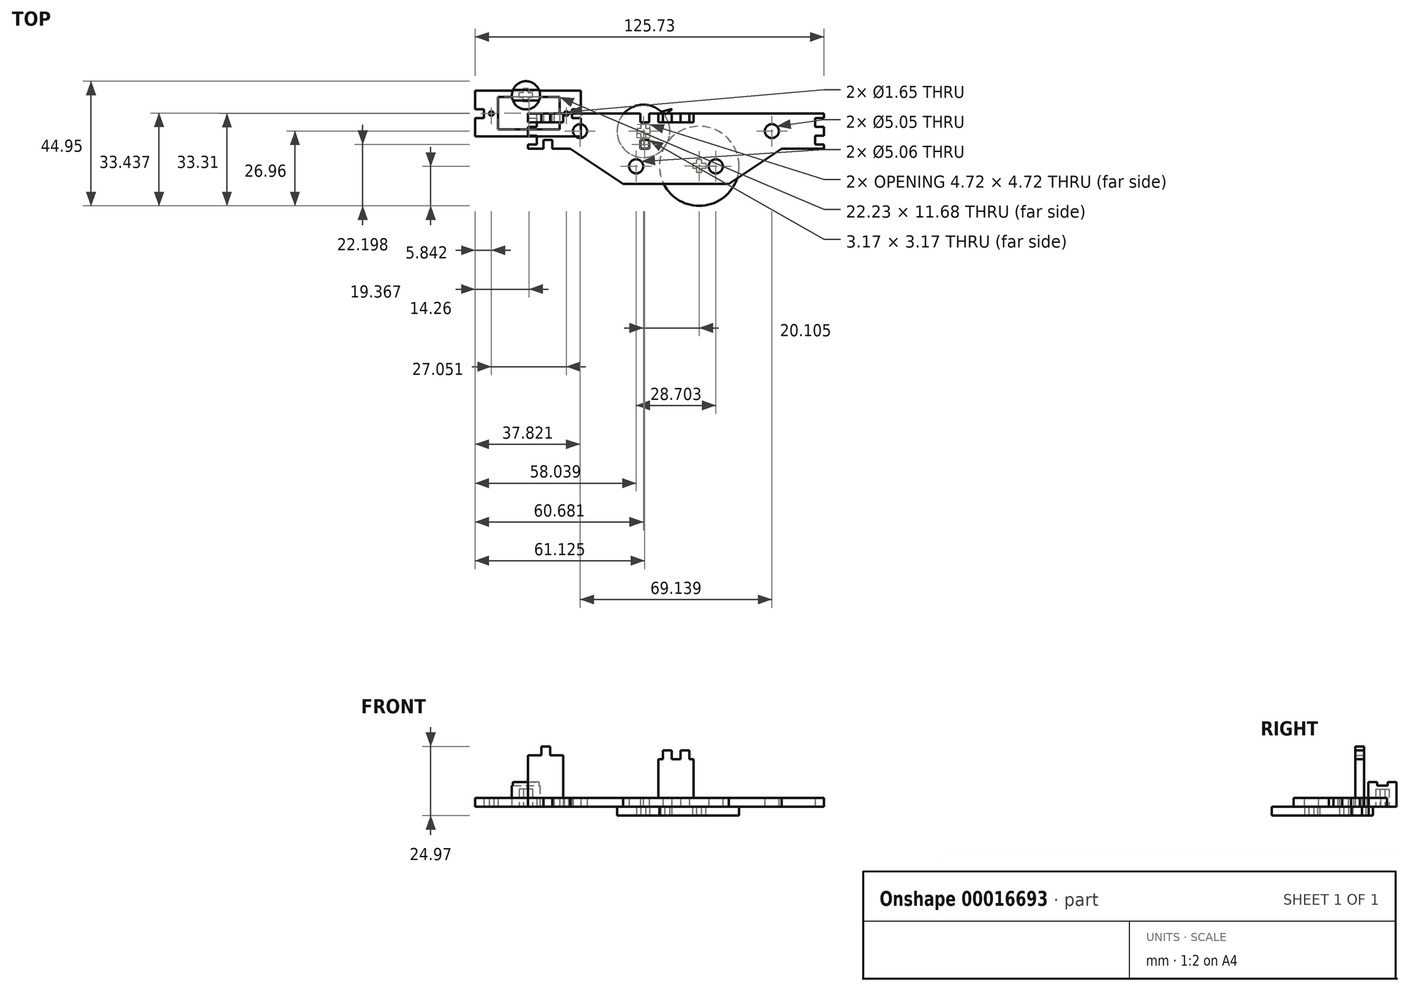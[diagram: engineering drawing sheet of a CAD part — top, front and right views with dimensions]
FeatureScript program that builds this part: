
annotation { "Feature Type Name" : "Feature", "Feature Type Description" : "" }
export const myFeature = defineFeature(function(context is Context, id is Id, definition is map)
    precondition{}
    {
        {
            var Q0;
            Q0=qCreatedBy(makeId("Top.planeOp"),FACE);
            var sketch = newSketch(context, id + "F0", { "sketchPlane" : qUnion([Q0])});
            skLineSegment(sketch, "E0.bottom", {"start": v(0, 0) * mm, "end": v(5.56, 0) * mm});
            skLineSegment(sketch, "E0.top", {"start": v(0, -12.7) * mm, "end": v(5.56, -12.7) * mm});
            skLineSegment(sketch, "E0.left", {"start": v(0, 0) * mm, "end": v(0, -12.7) * mm});
            skLineSegment(sketch, "E0.right", {"start": v(106.68, 0) * mm, "end": v(106.68, -12.7) * mm});
            skPoint(sketch, "E1", {"position": v(18.77, -6.35) * mm});
            skPoint(sketch, "E2", {"position": v(87.9, -6.35) * mm});
            skLineSegment(sketch, "E3", {"start": v(0, -6.35) * mm, "end": v(106.68, -6.35) * mm, "construction": true});
            skLineSegment(sketch, "E4.rect.bottom", {"start": v(19.66, -8.71) * mm, "end": v(17.88, -8.71) * mm});
            skLineSegment(sketch, "E4.rect.top", {"start": v(19.66, -3.99) * mm, "end": v(17.88, -3.99) * mm});
            skLineSegment(sketch, "E4.rect.left", {"start": v(19.66, -8.71) * mm, "end": v(19.66, -3.99) * mm});
            skLineSegment(sketch, "E4.rect.right", {"start": v(17.88, -8.71) * mm, "end": v(17.88, -3.99) * mm});
            skPoint(sketch, "E5.rect.middle", {"position": v(110.77, -6.35) * mm});
            skCircle(sketch, "E6", {"center": v(18.77, -6.35) * mm, "radius": 2.52 * mm});
            skPoint(sketch, "E7", {"position": v(53.34, -6.35) * mm});
            skLineSegment(sketch, "E8", {"start": v(15.24, -12.7) * mm, "end": v(34.3, -25.4) * mm});
            skLineSegment(sketch, "E9", {"start": v(34.3, -25.4) * mm, "end": v(72.4, -25.4) * mm});
            skLineSegment(sketch, "E10", {"start": v(72.4, -25.4) * mm, "end": v(91.44, -12.7) * mm});
            skLineSegment(sketch, "E11", {"start": v(18.77, -6.35) * mm, "end": v(87.9, -6.35) * mm});
            skCircle(sketch, "E12", {"center": v(38.99, -19.05) * mm, "radius": 2.53 * mm});
            skLineSegment(sketch, "E13", {"start": v(53.34, 9.16) * mm, "end": v(53.34, -37.34) * mm, "construction": true});
            skCircle(sketch, "E14.0.MirrorC", {"center": v(67.7, -19.05) * mm, "radius": 2.53 * mm});
            skCircle(sketch, "E15.0.MirrorC", {"center": v(87.9, -6.35) * mm, "radius": 2.52 * mm});
            skLineSegment(sketch, "E16.bottom", {"start": v(0, -1.59) * mm, "end": v(3.18, -1.59) * mm});
            skLineSegment(sketch, "E16.top", {"start": v(0, -4.76) * mm, "end": v(3.17, -4.76) * mm});
            skLineSegment(sketch, "E16.left", {"start": v(0, -1.59) * mm, "end": v(0, -4.76) * mm});
            skLineSegment(sketch, "E16.right", {"start": v(3.18, -1.59) * mm, "end": v(3.18, -4.76) * mm});
            skLineSegment(sketch, "E17.0.MirrorCS", {"start": v(0, -7.94) * mm, "end": v(3.17, -7.94) * mm});
            skLineSegment(sketch, "E18.0.MirrorCS", {"start": v(3.17, -11.11) * mm, "end": v(3.17, -7.94) * mm});
            skLineSegment(sketch, "E19.0.MirrorCS", {"start": v(0, -11.11) * mm, "end": v(3.18, -11.11) * mm});
            skLineSegment(sketch, "E20.0.MirrorCS", {"start": v(0, -11.11) * mm, "end": v(0, -7.94) * mm});
            skLineSegment(sketch, "E21.0.MirrorCS", {"start": v(103.5, -1.59) * mm, "end": v(103.5, -4.76) * mm});
            skLineSegment(sketch, "E22.0.MirrorCS", {"start": v(106.68, -1.59) * mm, "end": v(103.5, -1.59) * mm});
            skLineSegment(sketch, "E23.0.MirrorCS", {"start": v(106.68, -4.76) * mm, "end": v(103.5, -4.76) * mm});
            skLineSegment(sketch, "E24.0.MirrorCS", {"start": v(106.68, -1.59) * mm, "end": v(106.68, -4.76) * mm});
            skLineSegment(sketch, "E25.0.MirrorCS", {"start": v(106.68, -7.94) * mm, "end": v(103.5, -7.94) * mm});
            skLineSegment(sketch, "E26.0.MirrorCS", {"start": v(103.5, -11.11) * mm, "end": v(103.5, -7.94) * mm});
            skLineSegment(sketch, "E27.0.MirrorCS", {"start": v(106.68, -11.11) * mm, "end": v(103.5, -11.11) * mm});
            skLineSegment(sketch, "E28.0.MirrorCS", {"start": v(106.68, -11.11) * mm, "end": v(106.68, -7.94) * mm});
            skLineSegment(sketch, "E29", {"start": v(5.56, 0) * mm, "end": v(5.56, -3.18) * mm});
            skLineSegment(sketch, "E30", {"start": v(5.56, -3.18) * mm, "end": v(8.74, -3.18) * mm});
            skLineSegment(sketch, "E31", {"start": v(8.74, -3.18) * mm, "end": v(8.74, 0) * mm});
            skLineSegment(sketch, "E32", {"start": v(8.74, -12.7) * mm, "end": v(8.74, -9.52) * mm});
            skLineSegment(sketch, "E33", {"start": v(8.74, -9.52) * mm, "end": v(5.56, -9.52) * mm});
            skLineSegment(sketch, "E34", {"start": v(5.56, -9.52) * mm, "end": v(5.56, -12.7) * mm});
            skLineSegment(sketch, "E35.trimOffspring", {"start": v(8.74, 0) * mm, "end": v(40.49, 0) * mm});
            skLineSegment(sketch, "E36.trimOffspring", {"start": v(8.74, -12.7) * mm, "end": v(106.68, -12.7) * mm});
            skLineSegment(sketch, "E37", {"start": v(40.49, 0) * mm, "end": v(40.49, -3.18) * mm});
            skLineSegment(sketch, "E38", {"start": v(40.49, -3.18) * mm, "end": v(43.66, -3.18) * mm});
            skLineSegment(sketch, "E39", {"start": v(43.66, -3.18) * mm, "end": v(43.66, 0) * mm});
            skLineSegment(sketch, "E40", {"start": v(40.49, -12.7) * mm, "end": v(40.49, -9.52) * mm});
            skLineSegment(sketch, "E41", {"start": v(40.49, -9.52) * mm, "end": v(43.66, -9.52) * mm});
            skLineSegment(sketch, "E42", {"start": v(43.66, -9.52) * mm, "end": v(43.66, -12.7) * mm});
            skLineSegment(sketch, "E43.trimOffspring", {"start": v(43.66, 0) * mm, "end": v(106.68, 0) * mm});
            skLineSegment(sketch, "E44.top", {"start": v(51.75, -3.17) * mm, "end": v(48.58, -3.17) * mm});
            skLineSegment(sketch, "E44.left", {"start": v(51.75, 0) * mm, "end": v(51.75, -3.17) * mm});
            skLineSegment(sketch, "E44.right", {"start": v(48.58, 0) * mm, "end": v(48.58, -3.17) * mm});
            skLineSegment(sketch, "E45.top", {"start": v(54.93, -3.17) * mm, "end": v(58.1, -3.17) * mm});
            skLineSegment(sketch, "E45.left", {"start": v(54.93, 0) * mm, "end": v(54.93, -3.17) * mm});
            skLineSegment(sketch, "E45.right", {"start": v(58.1, 0) * mm, "end": v(58.1, -3.17) * mm});
            skPoint(sketch, "E46", {"position": v(53.34, 0) * mm});
            skSolve(sketch);
        }
        {
            var Q0;
            {var subQ3=sQuery(id+"F0.wireOp",EDGE,"E8");var subQ35=sQuery(id+"F0.wireOp",EDGE,"E0.bottom");Q0=qUnion([makeQuery(id+"F0.imprint","IMPRINT",FACE,{"disambiguationData":[TD([[makeQuery(id+"F0.imprint","IMPRINT",EDGE,{"derivedFrom":subQ3}),1.0]])]}),makeQuery(id+"F0.imprint","IMPRINT",FACE,{"disambiguationData":[TD([[makeQuery(id+"F0.imprint","IMPRINT",EDGE,{"derivedFrom":subQ35}),-1.0]])]})]);}
            extrude(context, id + "F1", {"entities" : qUnion([Q0]), "depth" : 3.17 * mm});
        }
        {
            var Q0;
            Q0=qCreatedBy(makeId("Top.planeOp"),FACE);
            var sketch = newSketch(context, id + "F2", { "sketchPlane" : qUnion([Q0])});
            skCircle(sketch, "E47", {"center": v(41.63, -6.35) * mm, "radius": 9.53 * mm});
            skLineSegment(sketch, "E48", {"start": v(49.38, -0.81) * mm, "end": v(51.92, 1.7) * mm});
            skLineSegment(sketch, "E49", {"start": v(51.92, 1.7) * mm, "end": v(48.03, 0.7) * mm});
            skLineSegment(sketch, "E50.rect.bottom", {"start": v(42.52, -8.71) * mm, "end": v(40.74, -8.71) * mm});
            skLineSegment(sketch, "E50.rect.top", {"start": v(42.52, -3.99) * mm, "end": v(40.74, -3.99) * mm});
            skLineSegment(sketch, "E50.rect.left", {"start": v(42.52, -8.71) * mm, "end": v(42.52, -3.99) * mm});
            skLineSegment(sketch, "E50.rect.right", {"start": v(40.74, -8.71) * mm, "end": v(40.74, -3.99) * mm});
            skLineSegment(sketch, "E51.rect.bottom", {"start": v(44, -5.46) * mm, "end": v(39.27, -5.46) * mm});
            skLineSegment(sketch, "E51.rect.top", {"start": v(44, -7.24) * mm, "end": v(39.27, -7.24) * mm});
            skLineSegment(sketch, "E51.rect.left", {"start": v(44, -5.46) * mm, "end": v(44, -7.24) * mm});
            skLineSegment(sketch, "E51.rect.right", {"start": v(39.27, -5.46) * mm, "end": v(39.27, -7.24) * mm});
            skSolve(sketch);
        }
        {
            var Q0;
            Q0=makeQuery(id+"F2.imprint","IMPRINT",FACE,{"disambiguationData":[TD([[makeQuery(id+"F2.imprint","IMPRINT",EDGE,{"derivedFrom":sQuery(id+"F2.wireOp",EDGE,"56dfebe2-708b-410e-807d-a486b5c591f2.0")}),-1.0]])]});
            var Q1;
            {var subQ11=sQuery(id+"F2.wireOp",EDGE,"E50.rect.bottom");Q1=makeQuery(id+"F2.imprint","IMPRINT",FACE,{"disambiguationData":[TD([[makeQuery(id+"F2.imprint","IMPRINT",EDGE,{"derivedFrom":subQ11}),1.0]])]});}
            var Q2;
            {var subQ1=sQuery(id+"F2.wireOp",EDGE,"E48");Q2=makeQuery(id+"F2.imprint","IMPRINT",FACE,{"disambiguationData":[TD([[makeQuery(id+"F2.imprint","IMPRINT",EDGE,{"derivedFrom":subQ1}),1.0]])]});}
            extrude(context, id + "F3", {"entities" : qUnion([Q0, Q1, Q2]), "oppositeDirection" : true, "depth" : 3.17 * mm});
        }
        {
            var Q0;
            Q0=qCreatedBy(makeId("Top.planeOp"),FACE);
            var sketch = newSketch(context, id + "F4", { "sketchPlane" : qUnion([Q0])});
            skLineSegment(sketch, "E52.rect.bottom", {"start": v(62.62, -21.32) * mm, "end": v(60.85, -21.32) * mm});
            skLineSegment(sketch, "E52.rect.top", {"start": v(62.62, -16.6) * mm, "end": v(60.85, -16.6) * mm});
            skLineSegment(sketch, "E52.rect.left", {"start": v(62.62, -21.32) * mm, "end": v(62.62, -16.6) * mm});
            skLineSegment(sketch, "E52.rect.right", {"start": v(60.85, -21.32) * mm, "end": v(60.85, -16.6) * mm});
            skPoint(sketch, "E52.rect.middle", {"position": v(61.74, -18.96) * mm});
            skLineSegment(sketch, "E53.rect.bottom", {"start": v(64.1, -18.07) * mm, "end": v(59.37, -18.07) * mm});
            skLineSegment(sketch, "E53.rect.top", {"start": v(64.1, -19.85) * mm, "end": v(59.37, -19.85) * mm});
            skLineSegment(sketch, "E53.rect.left", {"start": v(64.1, -18.07) * mm, "end": v(64.1, -19.85) * mm});
            skLineSegment(sketch, "E53.rect.right", {"start": v(59.37, -18.07) * mm, "end": v(59.37, -19.85) * mm});
            skCircle(sketch, "E54", {"center": v(61.74, -18.96) * mm, "radius": 14.35 * mm});
            skSolve(sketch);
        }
        {
            var Q0;
            {var subQ11=sQuery(id+"F4.wireOp",EDGE,"E52.rect.bottom");Q0=makeQuery(id+"F4.imprint","IMPRINT",FACE,{"disambiguationData":[TD([[makeQuery(id+"F4.imprint","IMPRINT",EDGE,{"derivedFrom":subQ11}),1.0]])]});}
            extrude(context, id + "F5", {"entities" : qUnion([Q0]), "oppositeDirection" : true, "depth" : 3.17 * mm});
        }
        {
            var Q0;
            Q0=qCreatedBy(makeId("Top.planeOp"),FACE);
            var sketch = newSketch(context, id + "F6", { "sketchPlane" : qUnion([Q0])});
            skCircle(sketch, "E55", {"center": v(-0.7, 6.56) * mm, "radius": 5.08 * mm});
            skLineSegment(sketch, "E56.rect.bottom", {"start": v(1.7, 5.67) * mm, "end": v(-3.12, 5.67) * mm});
            skLineSegment(sketch, "E56.rect.top", {"start": v(1.7, 7.45) * mm, "end": v(-3.12, 7.45) * mm});
            skLineSegment(sketch, "E56.rect.left", {"start": v(1.7, 5.67) * mm, "end": v(1.7, 7.45) * mm});
            skLineSegment(sketch, "E56.rect.right", {"start": v(-3.12, 5.67) * mm, "end": v(-3.12, 7.45) * mm});
            skLineSegment(sketch, "E57.rect.bottom", {"start": v(0.18, 4.15) * mm, "end": v(-1.6, 4.15) * mm});
            skLineSegment(sketch, "E57.rect.top", {"start": v(0.18, 8.97) * mm, "end": v(-1.6, 8.97) * mm});
            skLineSegment(sketch, "E57.rect.left", {"start": v(0.18, 4.15) * mm, "end": v(0.18, 8.97) * mm});
            skLineSegment(sketch, "E57.rect.right", {"start": v(-1.6, 4.15) * mm, "end": v(-1.6, 8.97) * mm});
            skSolve(sketch);
        }
        {
            var Q0;
            Q0=makeQuery(id+"F6.imprint","IMPRINT",FACE,{"disambiguationData":[TD([[makeQuery(id+"F6.imprint","IMPRINT",EDGE,{"derivedFrom":sQuery(id+"F6.wireOp",EDGE,"E55")}),1.0]])]});
            var Q1;
            {var subQ5=sQuery(id+"F6.wireOp",EDGE,"E56.rect.right");Q1=makeQuery(id+"F6.imprint","IMPRINT",FACE,{"disambiguationData":[TD([[makeQuery(id+"F6.imprint","IMPRINT",EDGE,{"derivedFrom":subQ5}),-1.0]])]});}
            var Q2;
            {var subQ3=sQuery(id+"F6.wireOp",EDGE,"E57.rect.top");Q2=makeQuery(id+"F6.imprint","IMPRINT",FACE,{"disambiguationData":[TD([[makeQuery(id+"F6.imprint","IMPRINT",EDGE,{"derivedFrom":subQ3}),1.0]])]});}
            var Q3;
            {var subQ3=sQuery(id+"F6.wireOp",EDGE,"E56.rect.bottom");var subQ5=sQuery(id+"F6.wireOp",EDGE,"E57.rect.left");var subQ7=makeQuery(id+"F6.imprint","INTERSECT",VERTEX,{"derivedFrom":[subQ3,subQ5]});Q3=makeQuery(id+"F6.imprint","IMPRINT",FACE,{"disambiguationData":[TD([[makeQuery(id+"F6.imprint","IMPRINT",EDGE,{"disambiguationData":[TD([[subQ7,-1.0]])],"derivedFrom":subQ3}),-1.0]])]});}
            var Q4;
            {var subQ3=sQuery(id+"F6.wireOp",EDGE,"E57.rect.bottom");Q4=makeQuery(id+"F6.imprint","IMPRINT",FACE,{"disambiguationData":[TD([[makeQuery(id+"F6.imprint","IMPRINT",EDGE,{"derivedFrom":subQ3}),-1.0]])]});}
            var Q5;
            {var subQ5=sQuery(id+"F6.wireOp",EDGE,"E56.rect.left");Q5=makeQuery(id+"F6.imprint","IMPRINT",FACE,{"disambiguationData":[TD([[makeQuery(id+"F6.imprint","IMPRINT",EDGE,{"derivedFrom":subQ5}),1.0]])]});}
            extrude(context, id + "F7", {"entities" : qUnion([Q0, Q1, Q2, Q3, Q4, Q5]), "depth" : 8.9 * mm});
        }
        {
            var Q0;
            {var subQ5=sQuery(id+"F6.wireOp",EDGE,"E56.rect.right");Q0=makeQuery(id+"F6.imprint","IMPRINT",FACE,{"disambiguationData":[TD([[makeQuery(id+"F6.imprint","IMPRINT",EDGE,{"derivedFrom":subQ5}),-1.0]])]});}
            var Q1;
            {var subQ3=sQuery(id+"F6.wireOp",EDGE,"E57.rect.top");Q1=makeQuery(id+"F6.imprint","IMPRINT",FACE,{"disambiguationData":[TD([[makeQuery(id+"F6.imprint","IMPRINT",EDGE,{"derivedFrom":subQ3}),1.0]])]});}
            var Q2;
            {var subQ3=sQuery(id+"F6.wireOp",EDGE,"E56.rect.bottom");var subQ5=sQuery(id+"F6.wireOp",EDGE,"E57.rect.left");var subQ7=makeQuery(id+"F6.imprint","INTERSECT",VERTEX,{"derivedFrom":[subQ3,subQ5]});Q2=makeQuery(id+"F6.imprint","IMPRINT",FACE,{"disambiguationData":[TD([[makeQuery(id+"F6.imprint","IMPRINT",EDGE,{"disambiguationData":[TD([[subQ7,-1.0]])],"derivedFrom":subQ3}),-1.0]])]});}
            var Q3;
            {var subQ3=sQuery(id+"F6.wireOp",EDGE,"E57.rect.bottom");Q3=makeQuery(id+"F6.imprint","IMPRINT",FACE,{"disambiguationData":[TD([[makeQuery(id+"F6.imprint","IMPRINT",EDGE,{"derivedFrom":subQ3}),-1.0]])]});}
            var Q4;
            {var subQ5=sQuery(id+"F6.wireOp",EDGE,"E56.rect.left");Q4=makeQuery(id+"F6.imprint","IMPRINT",FACE,{"disambiguationData":[TD([[makeQuery(id+"F6.imprint","IMPRINT",EDGE,{"derivedFrom":subQ5}),1.0]])]});}
            extrude(context, id + "F8", {"entities" : qUnion([Q0, Q1, Q2, Q3, Q4]), "operationType" : NewBodyOperationType.REMOVE, "depth" : 6.35 * mm});
        }
        {
            var Q0;
            Q0=makeQuery(id+"F7.opExtrude","CAP_FACE",FACE,{"disambiguationData":[OSD([sQuery(id+"F6.wireOp",EDGE,"E55")])],"isStart":false});
            var sketch = newSketch(context, id + "F9", { "sketchPlane" : qUnion([Q0])});
            skPoint(sketch, "E58.0", {"position": v(0, 0) * mm});
            skLineSegment(sketch, "E59.rect.bottom", {"start": v(-5.42, 8.47) * mm, "end": v(4, 8.47) * mm});
            skLineSegment(sketch, "E59.rect.top", {"start": v(-5.42, 4.66) * mm, "end": v(4, 4.66) * mm});
            skPoint(sketch, "E59.rect.middle", {"position": v(-0.7, 6.56) * mm});
            skArc(sketch, "E60.0", {"start": v(4, 4.66) * mm, "mid": v(4.37, 6.56) * mm, "end": v(4, 8.47) * mm});
            skArc(sketch, "E61.trimOffspring", {"start": v(-5.42, 8.47) * mm, "mid": v(-5.79, 6.56) * mm, "end": v(-5.42, 4.66) * mm});
            skSolve(sketch);
        }
        {
            var Q0;
            Q0=makeQuery(id+"F9.imprint","IMPRINT",FACE,{"disambiguationData":[TD([[makeQuery(id+"F9.imprint","IMPRINT",EDGE,{"derivedFrom":sQuery(id+"F9.wireOp",EDGE,"E59.rect.bottom")}),-1.0]])]});
            extrude(context, id + "F10", {"entities" : qUnion([Q0]), "operationType" : NewBodyOperationType.REMOVE, "oppositeDirection" : true, "depth" : 1.27 * mm});
        }
        {
            var Q0;
            Q0=qCreatedBy(makeId("Top.planeOp"),FACE);
            var sketch = newSketch(context, id + "F11", { "sketchPlane" : qUnion([Q0])});
            skLineSegment(sketch, "E62.rect.bottom", {"start": v(-19.05, 8.26) * mm, "end": v(19.05, 8.26) * mm});
            skLineSegment(sketch, "E62.rect.top", {"start": v(-19.05, -8.26) * mm, "end": v(19.05, -8.26) * mm});
            skLineSegment(sketch, "E62.rect.left", {"start": v(-19.05, 8.26) * mm, "end": v(-19.05, -8.25) * mm});
            skLineSegment(sketch, "E62.rect.right", {"start": v(19.05, 8.26) * mm, "end": v(19.05, -8.26) * mm});
            skPoint(sketch, "E62.rect.middle", {"position": v(0, 0) * mm});
            skCircle(sketch, "E63", {"center": v(5.84, 0) * mm, "radius": 5.59 * mm, "construction": true});
            skLineSegment(sketch, "E64.bottom", {"start": v(11.43, 5.97) * mm, "end": v(-10.8, 5.97) * mm});
            skLineSegment(sketch, "E64.top", {"start": v(11.43, -5.72) * mm, "end": v(-10.8, -5.72) * mm});
            skLineSegment(sketch, "E64.left", {"start": v(11.43, 5.97) * mm, "end": v(11.43, -5.72) * mm});
            skLineSegment(sketch, "E64.right", {"start": v(-10.8, 5.97) * mm, "end": v(-10.8, -5.72) * mm});
            skCircle(sketch, "E65", {"center": v(13.84, 0) * mm, "radius": 0.83 * mm});
            skCircle(sketch, "E66", {"center": v(-13.2, 0) * mm, "radius": 0.83 * mm});
            skLineSegment(sketch, "E67.bottom", {"start": v(19.05, -1.59) * mm, "end": v(15.87, -1.59) * mm});
            skLineSegment(sketch, "E67.top", {"start": v(19.05, 1.59) * mm, "end": v(15.87, 1.59) * mm});
            skLineSegment(sketch, "E67.left", {"start": v(19.05, -1.59) * mm, "end": v(19.05, 1.59) * mm});
            skLineSegment(sketch, "E67.right", {"start": v(15.87, -1.59) * mm, "end": v(15.87, 1.59) * mm});
            skLineSegment(sketch, "E68.bottom", {"start": v(-19.05, -1.59) * mm, "end": v(-15.88, -1.59) * mm});
            skLineSegment(sketch, "E68.top", {"start": v(-19.05, 1.59) * mm, "end": v(-15.88, 1.59) * mm});
            skLineSegment(sketch, "E68.left", {"start": v(-19.05, -1.59) * mm, "end": v(-19.05, 1.59) * mm});
            skLineSegment(sketch, "E68.right", {"start": v(-15.88, -1.59) * mm, "end": v(-15.88, 1.59) * mm});
            skPoint(sketch, "E69", {"position": v(19.05, 0) * mm});
            skLineSegment(sketch, "E70", {"start": v(5.84, -5.72) * mm, "end": v(5.84, 5.97) * mm, "construction": true});
            skSolve(sketch);
        }
        {
            var Q0;
            {var subQ6=sQuery(id+"F11.wireOp",EDGE,"E62.rect.bottom");Q0=makeQuery(id+"F11.imprint","IMPRINT",FACE,{"disambiguationData":[TD([[makeQuery(id+"F11.imprint","IMPRINT",EDGE,{"derivedFrom":subQ6}),-1.0]])]});}
            extrude(context, id + "F12", {"entities" : qUnion([Q0]), "depth" : 3.17 * mm});
        }
        {
            var Q0;
            Q0=qCreatedBy(makeId("Front.planeOp"),FACE);
            var sketch = newSketch(context, id + "F13", { "sketchPlane" : qUnion([Q0])});
            skLineSegment(sketch, "E71.bottom", {"start": v(7.94, 21.79) * mm, "end": v(4.76, 21.79) * mm});
            skLineSegment(sketch, "E71.top", {"start": v(12.7, 0) * mm, "end": v(9.52, 0) * mm});
            skLineSegment(sketch, "E71.left", {"start": v(12.7, 18.61) * mm, "end": v(12.7, 0) * mm});
            skLineSegment(sketch, "E71.right", {"start": v(0, 18.61) * mm, "end": v(0, 0) * mm});
            skLineSegment(sketch, "E72", {"start": v(4.76, 21.79) * mm, "end": v(4.76, 18.61) * mm});
            skLineSegment(sketch, "E73", {"start": v(4.76, 18.61) * mm, "end": v(0, 18.61) * mm});
            skLineSegment(sketch, "E74", {"start": v(7.94, 21.79) * mm, "end": v(7.94, 18.61) * mm});
            skLineSegment(sketch, "E75", {"start": v(7.94, 18.61) * mm, "end": v(12.7, 18.61) * mm});
            skPoint(sketch, "E76", {"position": v(6.35, 21.79) * mm});
            skPoint(sketch, "E77.orphan", {"position": v(0, 21.79) * mm});
            skPoint(sketch, "E78.orphan", {"position": v(12.7, 21.79) * mm});
            skLineSegment(sketch, "E79", {"start": v(0, 3.17) * mm, "end": v(3.18, 3.17) * mm});
            skLineSegment(sketch, "E80", {"start": v(3.18, 3.18) * mm, "end": v(3.18, 0) * mm});
            skLineSegment(sketch, "E81", {"start": v(9.52, 0) * mm, "end": v(9.52, 3.18) * mm});
            skLineSegment(sketch, "E82", {"start": v(9.52, 3.18) * mm, "end": v(12.7, 3.18) * mm});
            skLineSegment(sketch, "E83.trimOffspring", {"start": v(3.18, 0) * mm, "end": v(0, 0) * mm});
            skLineSegment(sketch, "E84", {"start": v(9.52, 3.18) * mm, "end": v(3.18, 3.17) * mm});
            skSolve(sketch);
        }
        {
            var Q0;
            Q0=makeQuery(id+"F13.imprint","IMPRINT",FACE,{"disambiguationData":[TD([[makeQuery(id+"F13.imprint","IMPRINT",EDGE,{"derivedFrom":sQuery(id+"F13.wireOp",EDGE,"E71.bottom")}),1.0]])]});
            var Q1;
            {var subQ2=sQuery(id+"F13.wireOp",EDGE,"E71.top");Q1=makeQuery(id+"F13.imprint","IMPRINT",FACE,{"disambiguationData":[TD([[makeQuery(id+"F13.imprint","IMPRINT",EDGE,{"derivedFrom":subQ2}),-1.0]])]});}
            var Q2;
            {var subQ1=sQuery(id+"F13.wireOp",EDGE,"E79");Q2=makeQuery(id+"F13.imprint","IMPRINT",FACE,{"disambiguationData":[TD([[makeQuery(id+"F13.imprint","IMPRINT",EDGE,{"derivedFrom":subQ1}),-1.0]])]});}
            extrude(context, id + "F14", {"entities" : qUnion([Q0, Q1, Q2]), "depth" : 3.17 * mm});
        }
        {
            var Q0;
            Q0=qCreatedBy(makeId("Front.planeOp"),FACE);
            var sketch = newSketch(context, id + "F15", { "sketchPlane" : qUnion([Q0])});
            skLineSegment(sketch, "E85.0", {"start": v(54.93, 3.18) * mm, "end": v(54.93, 0) * mm});
            skLineSegment(sketch, "E86.0", {"start": v(58.1, 3.18) * mm, "end": v(58.1, 0) * mm});
            skLineSegment(sketch, "E87.0", {"start": v(51.75, 3.18) * mm, "end": v(51.75, 0) * mm});
            skLineSegment(sketch, "E88.0", {"start": v(48.58, 3.18) * mm, "end": v(48.58, 0) * mm});
            skLineSegment(sketch, "E89.0", {"start": v(54.93, 0) * mm, "end": v(58.1, 0) * mm});
            skLineSegment(sketch, "E90.0", {"start": v(51.75, 3.18) * mm, "end": v(54.93, 3.18) * mm});
            skLineSegment(sketch, "E91.bottom", {"start": v(59.7, 3.18) * mm, "end": v(58.1, 3.18) * mm});
            skLineSegment(sketch, "E91.top", {"start": v(59.7, 17.15) * mm, "end": v(58.1, 17.15) * mm});
            skLineSegment(sketch, "E91.left", {"start": v(59.7, 3.18) * mm, "end": v(59.7, 17.15) * mm});
            skLineSegment(sketch, "E91.right", {"start": v(47, 3.18) * mm, "end": v(47, 17.15) * mm});
            skLineSegment(sketch, "E92.trimOffspring", {"start": v(54.93, 3.18) * mm, "end": v(51.75, 3.18) * mm});
            skLineSegment(sketch, "E93.trimOffspring", {"start": v(48.58, 3.18) * mm, "end": v(47, 3.18) * mm});
            skLineSegment(sketch, "E94", {"start": v(48.58, 0) * mm, "end": v(51.75, 0) * mm});
            skLineSegment(sketch, "E95", {"start": v(59.7, 10.16) * mm, "end": v(47, 10.16) * mm, "construction": true});
            skLineSegment(sketch, "E96.0.MirrorCS", {"start": v(54.93, 17.15) * mm, "end": v(54.93, 20.32) * mm});
            skLineSegment(sketch, "E97.0.MirrorCS", {"start": v(54.93, 20.32) * mm, "end": v(58.1, 20.32) * mm});
            skLineSegment(sketch, "E98.0.MirrorCS", {"start": v(58.1, 17.15) * mm, "end": v(58.1, 20.32) * mm});
            skLineSegment(sketch, "E99.0.MirrorCS", {"start": v(48.58, 17.15) * mm, "end": v(48.58, 20.32) * mm});
            skLineSegment(sketch, "E100.0.MirrorCS", {"start": v(48.58, 20.32) * mm, "end": v(51.75, 20.32) * mm});
            skLineSegment(sketch, "E101.0.MirrorCS", {"start": v(51.75, 17.15) * mm, "end": v(51.75, 20.32) * mm});
            skLineSegment(sketch, "E102.trimOffspring", {"start": v(54.93, 17.15) * mm, "end": v(51.75, 17.15) * mm});
            skLineSegment(sketch, "E103.trimOffspring", {"start": v(48.58, 17.15) * mm, "end": v(47, 17.15) * mm});
            skSolve(sketch);
        }
        {
            var Q0;
            Q0=makeQuery(id+"F15.imprint","IMPRINT",FACE,{"disambiguationData":[TD([[makeQuery(id+"F15.imprint","IMPRINT",EDGE,{"derivedFrom":sQuery(id+"F15.wireOp",EDGE,"E85.0")}),1.0]])]});
            extrude(context, id + "F16", {"entities" : qUnion([Q0]), "depth" : 3.17 * mm});
        }
    });
